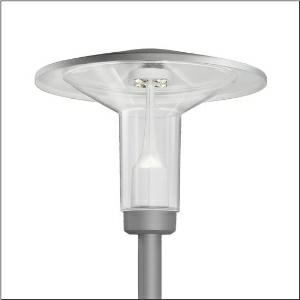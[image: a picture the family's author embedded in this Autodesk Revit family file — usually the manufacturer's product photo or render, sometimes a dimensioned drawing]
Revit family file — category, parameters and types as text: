
# Revit family: laterne_iq___st1_2a_5xa5255ef14h_6af0
name_source: partatom
category: Lighting Fixtures
units: mm (PartAtom-declared; Revit-internal decimal feet)

## family parameters
Cut with Voids When Loaded = No
Host = Face
Light Source = No
Part Type = Normal
Room Calculation Point = No
Round Connector Dimension = Use Diameter
Shared = No

## types (1)
- --- (1 x LED, 1540 lm, 10.5 W, 3000K)
    Apparent Load = 11 VA
    CIE Flux Codes = 25 63 94 98 100
    Color Rendering = 70
    Color Temperature = 3000K
    Default Elevation = 1800 mm
    Description = Lantern iQ, mast luminaire, Module 540 iQ-SR, primary light control with 3 zone facetted reflector, of plastic, silver coated, highly specular, structured, primary optical cover: cover, of PMMA, transparent, light distribution: ST1.2a, light emission: direct distribution, primary light characteristic: asymmetric, installation type: post-top, LED, High Power LED, rated luminous flux: 1.540lm, luminous efficacy: 147lm/W, light colour: 730, colour temperature: 3000K, control gear: iQ Street-Remote, control: Auto-Match, Temp-Guard, Lumen-Switch, Night-Set, Smart-Wire, Light-Fading, Desk-Remote (wireless, voltage-free reading and setting of iQ features in the workshop via application-optimized NFC function/RFID function), optimised constant luminous flux control (CLO 2.0), Street-Remote, pre-setting: logarithmic dimming characteristic, with terminal, 6-pole, max. 2.5mm², mains connection: 230..240V, AC, 50/60Hz, start of lifetime: 11W, end of service life: 11W, reduction: 5W, luminaire housing, upper part, of glass-fibre reinforced polyester, coated, Siteco® metallic grey (DB 702S), diameter: 750mm, height: 583mm, spigot size: d x l = 76 x 70mm (post-top) | with reducer (optional accessory) 60 x 70mm, mounting height: 3..5m, post-top mast mounting element, of diecast aluminium, coated, Siteco® metallic grey (DB 702S), Module 540 iQ-SR, traffic white (RAL 9016), equipment: standard, protection rating (complete): IP65, insulation class (complete): insulation class II (safety insulation), certification: CE, ENEC, VDE, packaging unit: 1 piece

Light Distribution: ST1.2a
    Height = 583 mm
    Lamp = 1 x LED
    Lamp Light Flux = 1540 lm
    Lamp Power = 10.5 W
    Lamp count = 1
    Length = 750 mm
    Luminous efficacy = 147 lm/W
    Manufacturer = Siteco
    ModVariant = No
    Model = 5XA5255EF14H
    Number of Poles = 1
    OnlyDefault = Yes
    Power Factor = 1
    Product Name = Laterne iQ | ST1.2a
    Product group = mast luminaire | pylon top
    ProductGroupID = 6100
    Protection Class = Protection class II
    Protection Degree = IP 65
    RLX_Detail_Level = 1
    RLX_Emergency_Light_Flux = 0 lm
    RLX_Emergency_Type = 0
    RLX_Emergency_Type_DB = No
    RlxData = <blob elided: 89581 chars, md5=1c3bbf39>
    Socket = socket
    Standby Power = 0 W
    System Light Flux = 1540 lm
    System Power = 11 W
    Type Comments = factory setting: luminous flux: 100 % | dim-lin: 254 | 419 mA
    Type Image = l_1006050.jpg
    URL = http://relux.com
    VarID = @adj_182101
    Voltage = 0 V
    Weight = 0.00 kg
    Width = 0 mm  [stored 0 ft]

note: [stored X ft] marks values corroborated as IEEE doubles in the binary element streams (Revit-internal decimal feet)

## geometry (parser evidence)
native form markers: Blend x4, Sweep x9
no freeform markers — native parametric forms only
